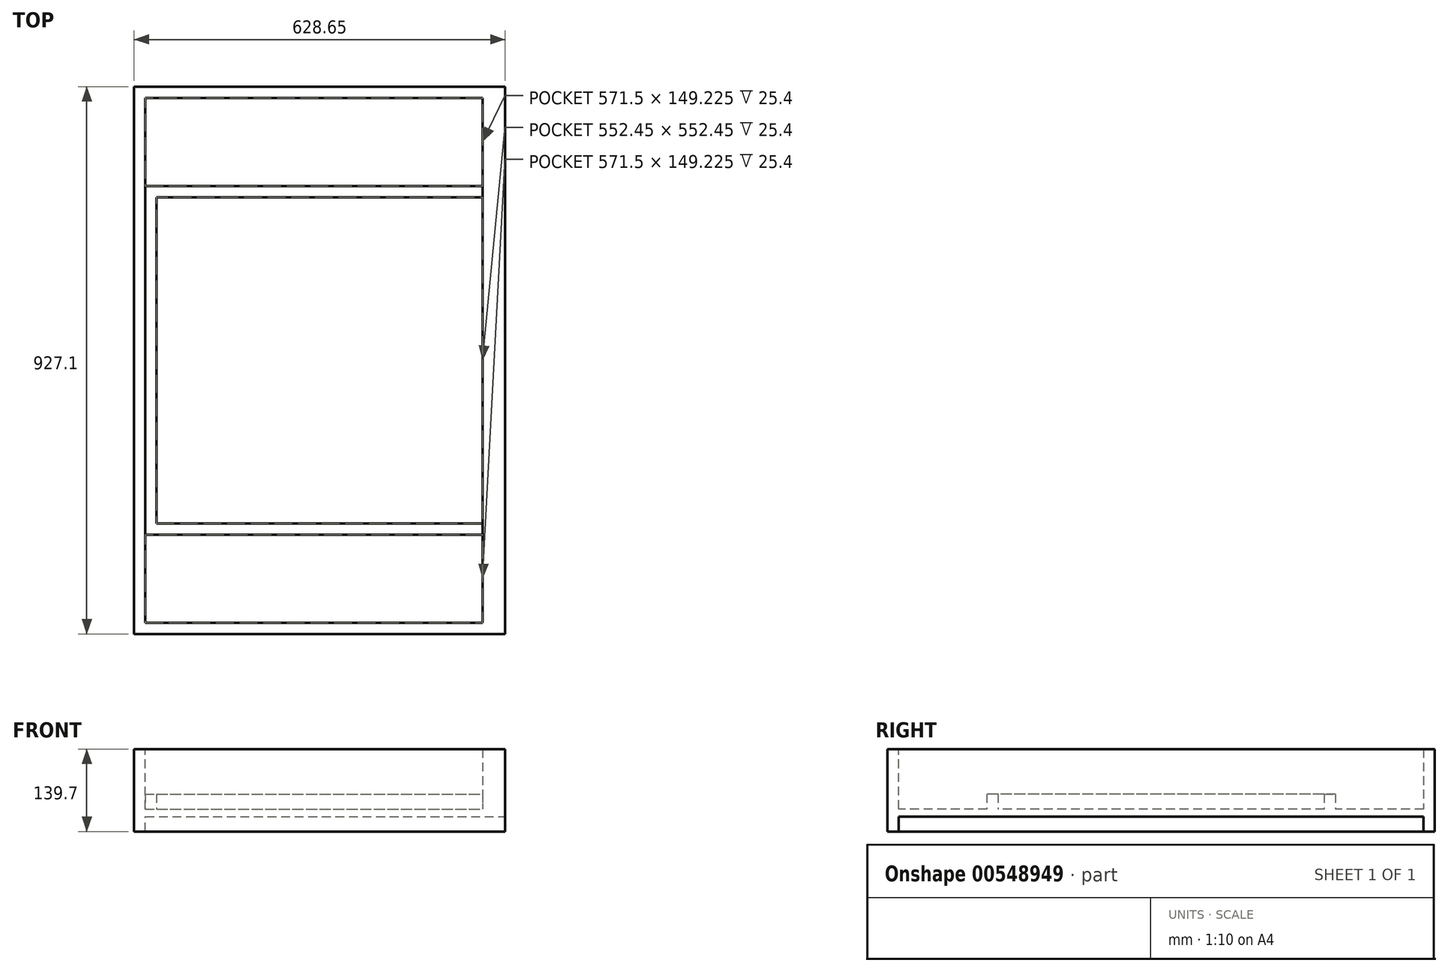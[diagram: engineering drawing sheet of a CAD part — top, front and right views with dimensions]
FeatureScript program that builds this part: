
annotation { "Feature Type Name" : "Feature", "Feature Type Description" : "" }
export const myFeature = defineFeature(function(context is Context, id is Id, definition is map)
    precondition{}
    {
        {
            var Q0;
            Q0=qCreatedBy(makeId("Top.planeOp"),FACE);
            var sketch = newSketch(context, id + "F0", { "sketchPlane" : qUnion([Q0])});
            skLineSegment(sketch, "E0.bottom", {"start": v(-304.8, 444.5) * mm, "end": v(304.8, 444.5) * mm});
            skLineSegment(sketch, "E0.top", {"start": v(-304.8, -444.5) * mm, "end": v(304.8, -444.5) * mm});
            skLineSegment(sketch, "E0.left", {"start": v(-304.8, 444.5) * mm, "end": v(-304.8, -444.5) * mm});
            skLineSegment(sketch, "E0.right", {"start": v(304.8, 444.5) * mm, "end": v(304.8, -444.5) * mm});
            skPoint(sketch, "E0.middle", {"position": v(0, 0) * mm});
            skSolve(sketch);
        }
        {
            var Q0;
            Q0=makeQuery(id+"F0.imprint","IMPRINT",FACE,{"disambiguationData":[TD([[makeQuery(id+"F0.imprint","IMPRINT",EDGE,{"derivedFrom":sQuery(id+"F0.wireOp",EDGE,"E0.bottom")}),-1.0]])]});
            extrude(context, id + "F1", {"entities" : qUnion([Q0]), "depth" : 12.7 * mm, "offsetDistance" : 25.4 * mm});
        }
        {
            var Q0;
            Q0=makeQuery(id+"F1.opExtrude","CAP_FACE",FACE,{"disambiguationData":[OSD([sQuery(id+"F0.wireOp",EDGE,"E0.bottom"),sQuery(id+"F0.wireOp",EDGE,"E0.top"),sQuery(id+"F0.wireOp",EDGE,"E0.left"),sQuery(id+"F0.wireOp",EDGE,"E0.right")])],"isStart":false});
            var sketch = newSketch(context, id + "F2", { "sketchPlane" : qUnion([Q0])});
            skPoint(sketch, "E1.middle", {"position": v(-9.53, 0) * mm});
            skLineSegment(sketch, "E2.bottom", {"start": v(-285.75, 276.23) * mm, "end": v(266.7, 276.23) * mm});
            skLineSegment(sketch, "E2.top", {"start": v(-285.75, -276.22) * mm, "end": v(266.7, -276.23) * mm});
            skLineSegment(sketch, "E2.left", {"start": v(-285.75, 276.23) * mm, "end": v(-285.75, -276.22) * mm});
            skLineSegment(sketch, "E3.bottom", {"start": v(-304.8, 295.28) * mm, "end": v(266.7, 295.28) * mm});
            skLineSegment(sketch, "E3.top", {"start": v(-304.8, -295.27) * mm, "end": v(266.7, -295.28) * mm});
            skLineSegment(sketch, "E3.left", {"start": v(-304.8, 295.28) * mm, "end": v(-304.8, -295.27) * mm});
            skLineSegment(sketch, "E3.right", {"start": v(304.8, 295.28) * mm, "end": v(304.8, -295.28) * mm, "construction": true});
            skPoint(sketch, "E3.middle", {"position": v(0, 0) * mm});
            skLineSegment(sketch, "E4", {"start": v(266.7, 276.23) * mm, "end": v(266.7, 295.28) * mm});
            skLineSegment(sketch, "E5", {"start": v(266.7, -276.22) * mm, "end": v(266.7, -295.28) * mm});
            skSolve(sketch);
        }
        {
            var Q0;
            Q0=makeQuery(id+"F2.imprint","IMPRINT",FACE,{"disambiguationData":[TD([[makeQuery(id+"F2.imprint","IMPRINT",EDGE,{"derivedFrom":sQuery(id+"F2.wireOp",EDGE,"E2.bottom")}),1.0]])]});
            extrude(context, id + "F3", {"entities" : qUnion([Q0]), "operationType" : NewBodyOperationType.ADD, "depth" : 25.4 * mm, "offsetDistance" : 25.4 * mm});
        }
        {
            var Q0;
            Q0=makeQuery(id+"F1.opExtrude","CAP_FACE",FACE,{"disambiguationData":[OSD([sQuery(id+"F0.wireOp",EDGE,"E0.bottom"),sQuery(id+"F0.wireOp",EDGE,"E0.top"),sQuery(id+"F0.wireOp",EDGE,"E0.left"),sQuery(id+"F0.wireOp",EDGE,"E0.right")])],"isStart":true});
            var sketch = newSketch(context, id + "F4", { "sketchPlane" : qUnion([Q0])});
            skLineSegment(sketch, "E6", {"start": v(304.8, 444.5) * mm, "end": v(-304.8, 444.5) * mm});
            skLineSegment(sketch, "E7", {"start": v(-304.8, 444.5) * mm, "end": v(-304.8, -444.5) * mm});
            skLineSegment(sketch, "E8", {"start": v(-304.8, -444.5) * mm, "end": v(304.8, -444.5) * mm});
            skLineSegment(sketch, "E9", {"start": v(304.8, -444.5) * mm, "end": v(304.8, -463.55) * mm});
            skLineSegment(sketch, "E10", {"start": v(304.8, -463.55) * mm, "end": v(-323.85, -463.55) * mm});
            skLineSegment(sketch, "E11", {"start": v(-323.85, -463.55) * mm, "end": v(-323.85, 463.55) * mm});
            skLineSegment(sketch, "E12", {"start": v(-323.85, 463.55) * mm, "end": v(304.8, 463.55) * mm});
            skLineSegment(sketch, "E13", {"start": v(304.8, 463.55) * mm, "end": v(304.8, 444.5) * mm});
            skSolve(sketch);
        }
        {
            var Q0;
            Q0=makeQuery(id+"F4.imprint","IMPRINT",FACE,{"disambiguationData":[TD([[makeQuery(id+"F4.imprint","IMPRINT",EDGE,{"derivedFrom":sQuery(id+"F4.wireOp",EDGE,"E6")}),1.0]])]});
            extrude(context, id + "F5", {"entities" : qUnion([Q0]), "operationType" : NewBodyOperationType.ADD, "depth" : 25.4 * mm, "offsetDistance" : 25.4 * mm, "hasSecondDirection" : true, "secondDirectionOppositeDirection" : true, "secondDirectionDepth" : 114.3 * mm});
        }
        {
            var Q0;
            Q0=makeQuery(id+"F1.opExtrude","CAP_FACE",FACE,{"disambiguationData":[OSD([sQuery(id+"F0.wireOp",EDGE,"E0.bottom"),sQuery(id+"F0.wireOp",EDGE,"E0.top"),sQuery(id+"F0.wireOp",EDGE,"E0.left"),sQuery(id+"F0.wireOp",EDGE,"E0.right")])],"isStart":false});
            var sketch = newSketch(context, id + "F6", { "sketchPlane" : qUnion([Q0])});
            skLineSegment(sketch, "E14.bottom", {"start": v(304.8, 444.5) * mm, "end": v(266.7, 444.5) * mm});
            skLineSegment(sketch, "E14.top", {"start": v(304.8, -444.5) * mm, "end": v(266.7, -444.5) * mm});
            skLineSegment(sketch, "E14.left", {"start": v(304.8, 444.5) * mm, "end": v(304.8, -444.5) * mm});
            skLineSegment(sketch, "E14.right", {"start": v(266.7, 444.5) * mm, "end": v(266.7, -444.5) * mm});
            skSolve(sketch);
        }
        {
            var Q0;
            {var subQ2=sQuery(id+"F6.wireOp",EDGE,"E14.bottom");Q0=makeQuery(id+"F6.imprint","IMPRINT",FACE,{"disambiguationData":[TD([[makeQuery(id+"F6.imprint","IMPRINT",EDGE,{"derivedFrom":subQ2}),-1.0]])]});}
            var Q1;
            Q1=makeQuery(id+"F5.opExtrude","CAP_FACE",FACE,{"disambiguationData":[OSD([sQuery(id+"F4.wireOp",EDGE,"E6"),sQuery(id+"F4.wireOp",EDGE,"E7"),sQuery(id+"F4.wireOp",EDGE,"E8"),sQuery(id+"F4.wireOp",EDGE,"E9"),sQuery(id+"F4.wireOp",EDGE,"E10"),sQuery(id+"F4.wireOp",EDGE,"E11"),sQuery(id+"F4.wireOp",EDGE,"E12"),sQuery(id+"F4.wireOp",EDGE,"E13")])],"isStart":true});
            extrude(context, id + "F7", {"entities" : qUnion([Q0]), "operationType" : NewBodyOperationType.ADD, "endBound" : BoundingType.UP_TO_SURFACE, "depth" : 25.4 * mm, "endBoundEntityFace" : qUnion([Q1]), "offsetDistance" : 25.4 * mm});
        }
    });
